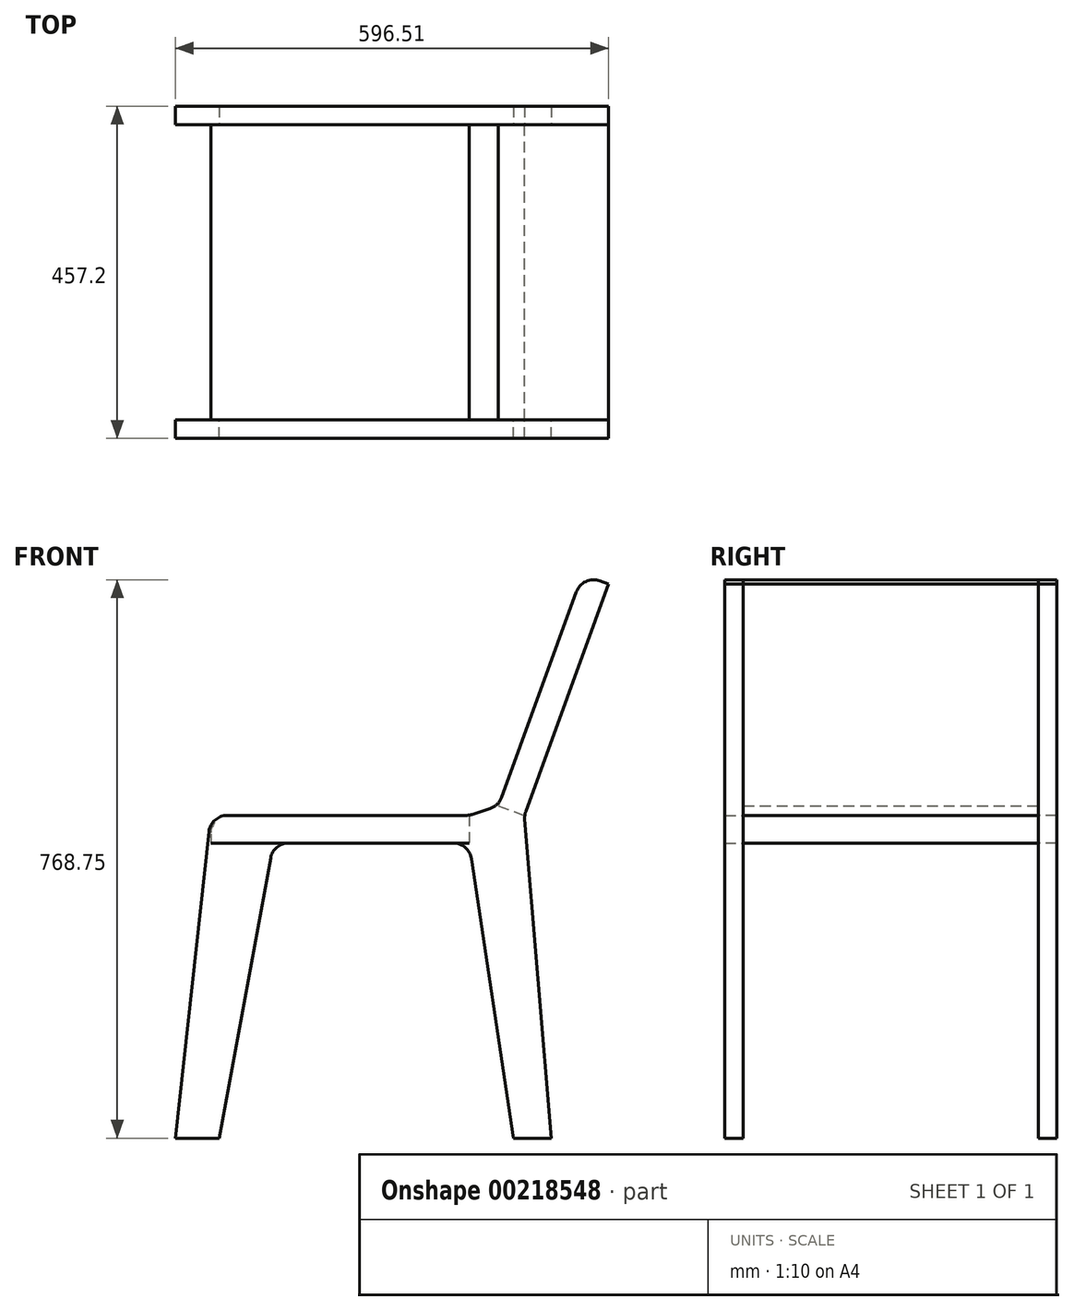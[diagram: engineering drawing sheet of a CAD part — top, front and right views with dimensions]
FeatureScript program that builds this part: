
annotation { "Feature Type Name" : "Feature", "Feature Type Description" : "" }
export const myFeature = defineFeature(function(context is Context, id is Id, definition is map)
    precondition{}
    {
        {
            var Q0;
            Q0=qCreatedBy(makeId("Front.planeOp"),FACE);
            var sketch = newSketch(context, id + "F0", { "sketchPlane" : qUnion([Q0])});
            skLineSegment(sketch, "E0.bottom", {"start": v(-152.4, 444.5) * mm, "end": v(203.2, 444.5) * mm});
            skLineSegment(sketch, "E0.top", {"start": v(-152.4, 406.4) * mm, "end": v(203.2, 406.4) * mm});
            skLineSegment(sketch, "E0.left", {"start": v(-152.4, 444.5) * mm, "end": v(-152.4, 406.4) * mm});
            skLineSegment(sketch, "E0.right", {"start": v(203.2, 444.5) * mm, "end": v(203.2, 406.4) * mm});
            skLineSegment(sketch, "E1", {"start": v(-152.4, 406.4) * mm, "end": v(-152.4, 0) * mm, "construction": true});
            skLineSegment(sketch, "E2", {"start": v(-152.4, 0) * mm, "end": v(203.2, 0) * mm, "construction": true});
            skLineSegment(sketch, "E3", {"start": v(203.2, 0) * mm, "end": v(203.2, 406.4) * mm, "construction": true});
            skLineSegment(sketch, "E4", {"start": v(359.48, 775.9) * mm, "end": v(243.6, 457.53) * mm});
            skLineSegment(sketch, "E5", {"start": v(243.6, 457.53) * mm, "end": v(279.4, 444.5) * mm});
            skLineSegment(sketch, "E6", {"start": v(279.4, 444.5) * mm, "end": v(395.28, 762.87) * mm});
            skLineSegment(sketch, "E7", {"start": v(395.28, 762.87) * mm, "end": v(359.48, 775.9) * mm});
            skLineSegment(sketch, "E8", {"start": v(203.2, 444.5) * mm, "end": v(279.4, 444.5) * mm, "construction": true});
            skSolve(sketch);
        }
        {
            var Q0;
            Q0=qSketchRegion(id+"F0",true);
            extrude(context, id + "F1", {"entities" : qUnion([Q0]), "depth" : 203.2 * mm, "hasSecondDirection" : true, "secondDirectionOppositeDirection" : true, "secondDirectionDepth" : 203.2 * mm});
        }
        {
            var Q0;
            Q0=makeQuery(id+"F1.opExtrude","CAP_FACE",FACE,{"disambiguationData":[OSD([sQuery(id+"F0.wireOp",EDGE,"E0.bottom"),sQuery(id+"F0.wireOp",EDGE,"E0.top"),sQuery(id+"F0.wireOp",EDGE,"E0.left"),sQuery(id+"F0.wireOp",EDGE,"E0.right")])],"isStart":false});
            cPlane(context, id + "F2", {"entities" : qUnion([Q0]), "cplaneType" : CPlaneType.OFFSET, "offset" : 0 * mm, "width" : 152.4 * mm, "height" : 152.4 * mm});
        }
        {
            var Q0;
            Q0=qCreatedBy(id+"F2.planeOp",FACE);
            var sketch = newSketch(context, id + "F3", { "sketchPlane" : qUnion([Q0])});
            skLineSegment(sketch, "E9.0", {"start": v(279.4, 444.5) * mm, "end": v(395.28, 762.87) * mm});
            skLineSegment(sketch, "E10.0.0", {"start": v(395.28, 762.87) * mm, "end": v(359.48, 775.9) * mm});
            skLineSegment(sketch, "E10.0.1", {"start": v(359.48, 775.9) * mm, "end": v(243.6, 457.53) * mm});
            skLineSegment(sketch, "E11.0.0", {"start": v(203.2, 444.5) * mm, "end": v(-152.4, 444.5) * mm});
            skLineSegment(sketch, "E12", {"start": v(279.4, 444.5) * mm, "end": v(316.34, 0) * mm});
            skLineSegment(sketch, "E13", {"start": v(316.34, 0) * mm, "end": v(264.09, 0) * mm});
            skLineSegment(sketch, "E14", {"start": v(264.09, 0) * mm, "end": v(203.2, 406.4) * mm});
            skLineSegment(sketch, "E15", {"start": v(203.2, 406.4) * mm, "end": v(-66.1, 406.4) * mm});
            skLineSegment(sketch, "E16", {"start": v(-66.1, 406.4) * mm, "end": v(-140.75, 0) * mm});
            skLineSegment(sketch, "E17", {"start": v(-140.75, 0) * mm, "end": v(-201.23, 0) * mm});
            skLineSegment(sketch, "E18", {"start": v(-201.23, 0) * mm, "end": v(-152.4, 444.5) * mm});
            skLineSegment(sketch, "E19", {"start": v(203.2, 444.5) * mm, "end": v(243.6, 457.53) * mm});
            skSolve(sketch);
        }
        {
            var Q0;
            Q0=makeQuery(id+"F3.imprint","IMPRINT",FACE,{"disambiguationData":[TD([[makeQuery(id+"F3.imprint","IMPRINT",EDGE,{"derivedFrom":sQuery(id+"F3.wireOp",EDGE,"E11.0.0")}),-1.0]])]});
            var Q1;
            {var subQ2=sQuery(id+"F3.wireOp",EDGE,"E16");Q1=makeQuery(id+"F3.imprint","IMPRINT",FACE,{"disambiguationData":[TD([[makeQuery(id+"F3.imprint","IMPRINT",EDGE,{"derivedFrom":subQ2}),-1.0]])]});}
            var Q2;
            Q2=makeQuery(id+"F3.imprint","IMPRINT",FACE,{"disambiguationData":[TD([[makeQuery(id+"F3.imprint","IMPRINT",EDGE,{"derivedFrom":sQuery(id+"F3.wireOp",EDGE,"E10.0.0")}),1.0]])]});
            extrude(context, id + "F4", {"entities" : qUnion([Q0, Q1, Q2]), "depth" : 25.4 * mm});
        }
        {
            var Q0;
            Q0=makeQuery(id+"F1.opExtrude","SWEPT_EDGE",EDGE,{"disambiguationData":[OSD([sQuery(id+"F0.wireOp",EDGE,"E0.bottom"),sQuery(id+"F0.wireOp",EDGE,"E0.left")])]});
            var Q1;
            Q1=makeQuery(id+"F6.opPattern","COPY",EDGE,{"derivedFrom":makeQuery(id+"F4.opExtrude","SWEPT_EDGE",EDGE,{"disambiguationData":[OSD([sQuery(id+"F3.wireOp",EDGE,"E11.0.0"),sQuery(id+"F3.wireOp",EDGE,"E18")])]}),"instanceName":"1"});
            var Q2;
            Q2=makeQuery(id+"F4.opExtrude","SWEPT_EDGE",EDGE,{"disambiguationData":[OSD([sQuery(id+"F3.wireOp",EDGE,"E11.0.0"),sQuery(id+"F3.wireOp",EDGE,"E18")])]});
            var Q3;
            Q3=makeQuery(id+"F4.opExtrude","SWEPT_EDGE",EDGE,{"disambiguationData":[OSD([sQuery(id+"F3.wireOp",EDGE,"E10.0.0"),sQuery(id+"F3.wireOp",EDGE,"E10.0.1")])]});
            var Q4;
            Q4=makeQuery(id+"F1.opExtrude","SWEPT_EDGE",EDGE,{"disambiguationData":[OSD([sQuery(id+"F0.wireOp",EDGE,"E4"),sQuery(id+"F0.wireOp",EDGE,"E7")])]});
            var Q5;
            Q5=makeQuery(id+"F6.opPattern","COPY",EDGE,{"derivedFrom":makeQuery(id+"F4.opExtrude","SWEPT_EDGE",EDGE,{"disambiguationData":[OSD([sQuery(id+"F3.wireOp",EDGE,"E10.0.0"),sQuery(id+"F3.wireOp",EDGE,"E10.0.1")])]}),"instanceName":"1"});
            var Q6;
            Q6=makeQuery(id+"F4.opExtrude","SWEPT_EDGE",EDGE,{"disambiguationData":[OSD([sQuery(id+"F3.wireOp",EDGE,"E11.0.0"),sQuery(id+"F3.wireOp",EDGE,"E19")])]});
            var Q7;
            Q7=makeQuery(id+"F4.opExtrude","SWEPT_EDGE",EDGE,{"disambiguationData":[OSD([sQuery(id+"F3.wireOp",EDGE,"E10.0.1"),sQuery(id+"F3.wireOp",EDGE,"E19")])]});
            var Q8;
            Q8=makeQuery(id+"F6.opPattern","COPY",EDGE,{"derivedFrom":makeQuery(id+"F4.opExtrude","SWEPT_EDGE",EDGE,{"disambiguationData":[OSD([sQuery(id+"F3.wireOp",EDGE,"E11.0.0"),sQuery(id+"F3.wireOp",EDGE,"E19")])]}),"instanceName":"1"});
            var Q9;
            Q9=makeQuery(id+"F6.opPattern","COPY",EDGE,{"derivedFrom":makeQuery(id+"F4.opExtrude","SWEPT_EDGE",EDGE,{"disambiguationData":[OSD([sQuery(id+"F3.wireOp",EDGE,"E10.0.1"),sQuery(id+"F3.wireOp",EDGE,"E19")])]}),"instanceName":"1"});
            var Q10;
            Q10=makeQuery(id+"F4.opExtrude","SWEPT_EDGE",EDGE,{"disambiguationData":[OSD([sQuery(id+"F3.wireOp",EDGE,"E9.0"),sQuery(id+"F3.wireOp",EDGE,"E12")])]});
            var Q11;
            Q11=makeQuery(id+"F6.opPattern","COPY",EDGE,{"derivedFrom":makeQuery(id+"F4.opExtrude","SWEPT_EDGE",EDGE,{"disambiguationData":[OSD([sQuery(id+"F3.wireOp",EDGE,"E9.0"),sQuery(id+"F3.wireOp",EDGE,"E12")])]}),"instanceName":"1"});
            var Q12;
            Q12=makeQuery(id+"F4.opExtrude","SWEPT_EDGE",EDGE,{"disambiguationData":[OSD([sQuery(id+"F3.wireOp",EDGE,"E14"),sQuery(id+"F3.wireOp",EDGE,"E15")])]});
            var Q13;
            Q13=makeQuery(id+"F4.opExtrude","SWEPT_EDGE",EDGE,{"disambiguationData":[OSD([sQuery(id+"F3.wireOp",EDGE,"E15"),sQuery(id+"F3.wireOp",EDGE,"E16")])]});
            fillet(context, id + "F5", {"entities" : qUnion([Q0, Q1, Q2, Q3, Q4, Q5, Q6, Q7, Q8, Q9, Q10, Q11, Q12, Q13]), "radius" : 25.4 * mm, "tangentPropagation" : true, "allowEdgeOverflow" : false});
        }
        {
            var Q0;
            Q0=makeQuery(id+"F4.opExtrude","SWEPT_BODY",BODY,{"disambiguationData":[OSD([sQuery(id+"F3.wireOp",EDGE,"E10.0.0"),sQuery(id+"F3.wireOp",EDGE,"E10.0.1"),sQuery(id+"F3.wireOp",EDGE,"E9.0"),sQuery(id+"F3.wireOp",EDGE,"E11.0.0"),sQuery(id+"F3.wireOp",EDGE,"E12"),sQuery(id+"F3.wireOp",EDGE,"E13"),sQuery(id+"F3.wireOp",EDGE,"E14"),sQuery(id+"F3.wireOp",EDGE,"E15"),sQuery(id+"F3.wireOp",EDGE,"E16"),sQuery(id+"F3.wireOp",EDGE,"E17"),sQuery(id+"F3.wireOp",EDGE,"E18"),sQuery(id+"F3.wireOp",EDGE,"E19")])]});
            var Q1;
            Q1=qCreatedBy(makeId("Front.planeOp"),FACE);
            mirror(context, id + "F6", {"entities" : qUnion([Q0]), "mirrorPlane" : qUnion([Q1])});
        }
    });
